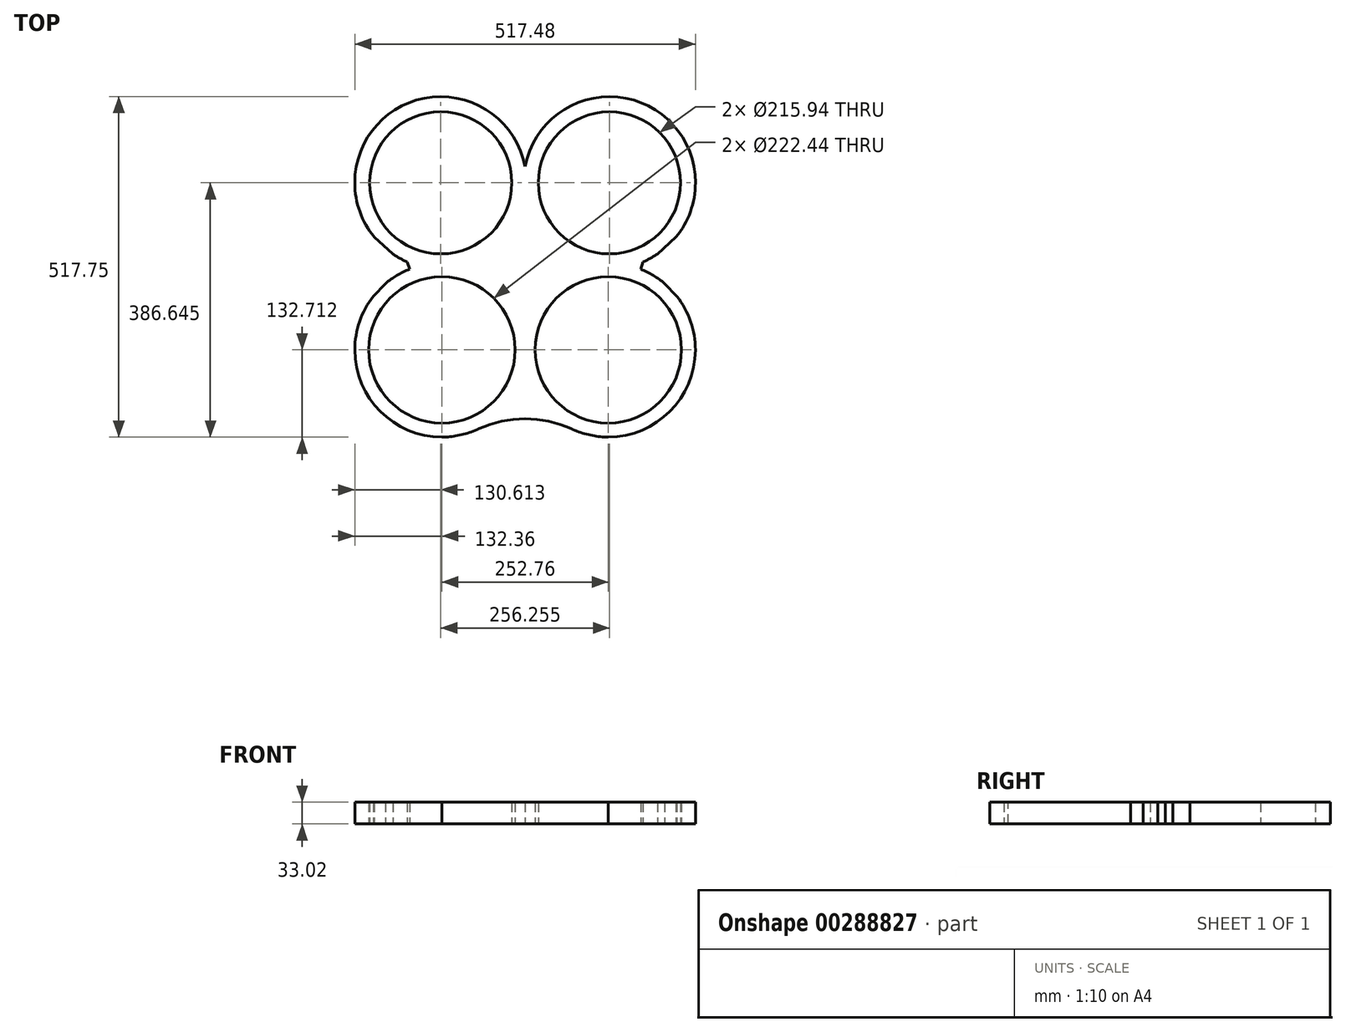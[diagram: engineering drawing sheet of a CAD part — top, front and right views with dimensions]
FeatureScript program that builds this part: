
annotation { "Feature Type Name" : "Feature", "Feature Type Description" : "" }
export const myFeature = defineFeature(function(context is Context, id is Id, definition is map)
    precondition{}
    {
        {
            var Q0;
            Q0=qCreatedBy(makeId("Top.planeOp"),FACE);
            var sketch = newSketch(context, id + "F0", { "sketchPlane" : qUnion([Q0])});
            skLineSegment(sketch, "E0.bottom", {"start": v(258.5, -258.5) * mm, "end": v(-258.5, -258.5) * mm});
            skLineSegment(sketch, "E0.top", {"start": v(258.5, 258.5) * mm, "end": v(-258.5, 258.5) * mm});
            skLineSegment(sketch, "E0.left", {"start": v(258.5, -258.5) * mm, "end": v(258.5, 258.5) * mm});
            skLineSegment(sketch, "E0.right", {"start": v(-258.5, -258.5) * mm, "end": v(-258.5, 258.5) * mm});
            skPoint(sketch, "E0.middle", {"position": v(0, 0) * mm});
            skSolve(sketch);
        }
        {
            var Q0;
            Q0=makeQuery(id+"F0.imprint","IMPRINT",FACE,{"disambiguationData":[TD([[makeQuery(id+"F0.imprint","IMPRINT",EDGE,{"derivedFrom":sQuery(id+"F0.wireOp",EDGE,"E0.bottom")}),-1.0]])]});
            var sketch = newSketch(context, id + "F1", { "sketchPlane" : qUnion([Q0])});
            skLineSegment(sketch, "E1.right", {"start": v(258.7, 258.65) * mm, "end": v(258.7, -258.65) * mm});
            skPoint(sketch, "E1.middle", {"position": v(0, 0) * mm});
            skPoint(sketch, "E2", {"position": v(0, 258.65) * mm});
            skLineSegment(sketch, "E3", {"start": v(0, -258.65) * mm, "end": v(0, 258.65) * mm, "construction": true});
            skCircle(sketch, "E4", {"center": v(-128.11, 128.05) * mm, "radius": 130.6 * mm});
            skCircle(sketch, "E5", {"center": v(-126.35, -125.94) * mm, "radius": 132.36 * mm});
            skPoint(sketch, "E6", {"position": v(-126.29, -258.65) * mm});
            skPoint(sketch, "E7", {"position": v(-258.7, -125.94) * mm});
            skPoint(sketch, "E8", {"position": v(-128.11, 258.65) * mm});
            skPoint(sketch, "E9", {"position": v(-258.7, 128.06) * mm});
            skLineSegment(sketch, "E10", {"start": v(-229.23, 45.4) * mm, "end": v(-230.7, -44.52) * mm});
            skLineSegment(sketch, "E11", {"start": v(-200.91, 19.63) * mm, "end": v(-212.36, -25.34) * mm});
            skLineSegment(sketch, "E12", {"start": v(-179.16, 7.84) * mm, "end": v(-175.56, -3.06) * mm});
            skCircle(sketch, "E13", {"center": v(-128.11, 128.05) * mm, "radius": 108 * mm});
            skCircle(sketch, "E14", {"center": v(-126.35, -125.94) * mm, "radius": 110.8 * mm});
            skLineSegment(sketch, "E15", {"start": v(-78.82, -249.47) * mm, "end": v(0, -230.92) * mm});
            skCircle(sketch, "E16.MirrorC", {"center": v(128.11, 128.05) * mm, "radius": 130.6 * mm});
            skCircle(sketch, "E17.MirrorC", {"center": v(128.11, 128.05) * mm, "radius": 108 * mm});
            skLineSegment(sketch, "E18.MirrorCS", {"start": v(179.16, 7.84) * mm, "end": v(175.56, -3.06) * mm});
            skPoint(sketch, "E19.MirrorP", {"position": v(128.11, 258.65) * mm});
            skPoint(sketch, "E20.MirrorP", {"position": v(126.29, -258.65) * mm});
            skLineSegment(sketch, "E21.MirrorCS", {"start": v(229.23, 45.4) * mm, "end": v(230.7, -44.52) * mm});
            skLineSegment(sketch, "E22.MirrorCS", {"start": v(200.91, 19.63) * mm, "end": v(212.36, -25.34) * mm});
            skPoint(sketch, "E23.MirrorP", {"position": v(258.7, 128.06) * mm});
            skCircle(sketch, "E24.MirrorC", {"center": v(126.35, -125.94) * mm, "radius": 132.36 * mm});
            skCircle(sketch, "E25.MirrorC", {"center": v(126.35, -125.94) * mm, "radius": 110.8 * mm});
            skLineSegment(sketch, "E26.MirrorCS", {"start": v(78.82, -249.47) * mm, "end": v(0, -230.92) * mm});
            skPoint(sketch, "E27.MirrorP", {"position": v(258.7, -125.94) * mm});
            skSolve(sketch);
        }
        {
            var Q0;
            Q0=qCreatedBy(makeId("Top.planeOp"),FACE);
            var sketch = newSketch(context, id + "F2", { "sketchPlane" : qUnion([Q0])});
            skCircle(sketch, "E28", {"center": v(-128.13, 128.02) * mm, "radius": 107.97 * mm});
            skCircle(sketch, "E29", {"center": v(-126.38, -125.92) * mm, "radius": 111.22 * mm});
            skArc(sketch, "E30", {"start": v(-258.74, -125.94) * mm, "mid": v(-219.84, -219.58) * mm, "end": v(-126.26, -258.63) * mm});
            skArc(sketch, "E31", {"start": v(-230.73, -44.37) * mm, "mid": v(-251.44, -82.85) * mm, "end": v(-258.74, -125.94) * mm});
            skArc(sketch, "E32", {"start": v(-175.52, -3.13) * mm, "mid": v(-194.8, -12.7) * mm, "end": v(-212.3, -25.24) * mm});
            skArc(sketch, "E33", {"start": v(-200.91, 19.73) * mm, "mid": v(-190.27, 13.3) * mm, "end": v(-179.09, 7.87) * mm});
            skArc(sketch, "E34", {"start": v(-258.74, 128.08) * mm, "mid": v(-251.19, 84.19) * mm, "end": v(-229.21, 45.45) * mm});
            skArc(sketch, "E35", {"start": v(0, 153.02) * mm, "mid": v(-140.74, 258.51) * mm, "end": v(-258.74, 128.08) * mm});
            skArc(sketch, "E36", {"start": v(-126.26, -258.63) * mm, "mid": v(-102.18, -256.06) * mm, "end": v(-78.86, -249.51) * mm});
            skLineSegment(sketch, "E37", {"start": v(-179.09, 7.87) * mm, "end": v(-175.52, -3.13) * mm});
            skArc(sketch, "E38.MirrorCS", {"start": v(0, 153.02) * mm, "mid": v(140.74, 258.51) * mm, "end": v(258.74, 128.08) * mm});
            skCircle(sketch, "E39.MirrorC", {"center": v(128.13, 128.02) * mm, "radius": 107.97 * mm});
            skArc(sketch, "E40.MirrorCS", {"start": v(258.74, 128.08) * mm, "mid": v(251.19, 84.19) * mm, "end": v(229.21, 45.45) * mm});
            skArc(sketch, "E41.MirrorCS", {"start": v(200.91, 19.73) * mm, "mid": v(190.27, 13.3) * mm, "end": v(179.09, 7.87) * mm});
            skLineSegment(sketch, "E42.MirrorCS", {"start": v(179.09, 7.87) * mm, "end": v(175.52, -3.13) * mm});
            skArc(sketch, "E43.MirrorCS", {"start": v(175.52, -3.13) * mm, "mid": v(194.8, -12.7) * mm, "end": v(212.3, -25.24) * mm});
            skCircle(sketch, "E44.MirrorC", {"center": v(126.38, -125.92) * mm, "radius": 111.22 * mm});
            skArc(sketch, "E45.MirrorCS", {"start": v(126.26, -258.63) * mm, "mid": v(102.18, -256.06) * mm, "end": v(78.86, -249.51) * mm});
            skArc(sketch, "E46.MirrorCS", {"start": v(258.74, -125.94) * mm, "mid": v(219.84, -219.58) * mm, "end": v(126.26, -258.63) * mm});
            skArc(sketch, "E47.MirrorCS", {"start": v(230.73, -44.37) * mm, "mid": v(251.44, -82.85) * mm, "end": v(258.74, -125.94) * mm});
            skLineSegment(sketch, "E48", {"start": v(200.91, 19.73) * mm, "end": v(229.21, 45.45) * mm});
            skLineSegment(sketch, "E49", {"start": v(212.3, -25.24) * mm, "end": v(230.73, -44.37) * mm});
            skLineSegment(sketch, "E50", {"start": v(-200.91, 19.73) * mm, "end": v(-229.21, 45.45) * mm});
            skLineSegment(sketch, "E51", {"start": v(-212.3, -25.24) * mm, "end": v(-230.73, -44.37) * mm});
            skArc(sketch, "E52", {"start": v(-78.86, -249.51) * mm, "mid": v(-29.57, -216.55) * mm, "end": v(0, -165.15) * mm});
            skArc(sketch, "E53", {"start": v(0, -165.15) * mm, "mid": v(29.56, -216.55) * mm, "end": v(78.86, -249.51) * mm});
            skSolve(sketch);
        }
        {
            var Q0;
            Q0 = qSketchRegion(id + "F2", true);
            extrude(context, id + "F3", {"entities" : qUnion([Q0]), "depth" : 33.02 * mm});
        }
        {
            var Q0;
            Q0=makeQuery(id+"F3.opExtrude","SWEPT_EDGE",EDGE,{"disambiguationData":[OSD([sQuery(id+"F2.wireOp",EDGE,"E52"),sQuery(id+"F2.wireOp",EDGE,"E53")])]});
            fillet(context, id + "F4", {"entities" : qUnion([Q0]), "radius" : 168.54 * mm, "tangentPropagation" : true, "allowEdgeOverflow" : false});
        }
    });
